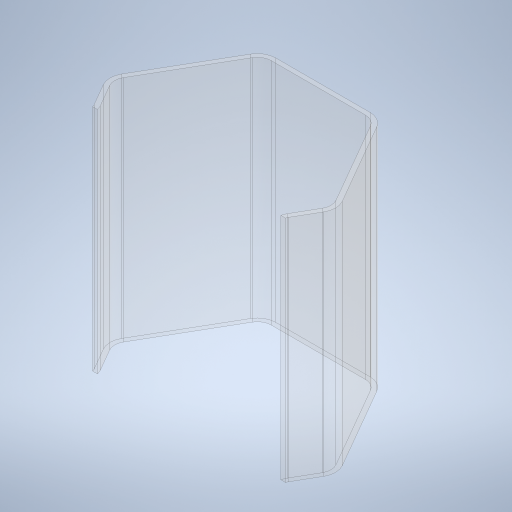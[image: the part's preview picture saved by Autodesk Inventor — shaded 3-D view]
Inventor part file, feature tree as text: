
AUTODESK INVENTOR PART (.ipt)
format: ipt  version: 2024 (Build 280153000, 153)  size: 451,584 bytes
history: native  units: mm
features: extrude x9, sketch x9, projected_geometry x3, fillet x1
ambient origin geometry x8: Origin, YZ Plane, XZ Plane, XY Plane, X Axis, Y Axis, Z Axis, Center Point
bodies: Solid1 (feature_tree)
feature tree (22):
  extrude  "Extrusion1"  Depth=10.0mm
  extrude  "Extrusion2"  Depth=20.0mm TaperAngle=0.0deg
  sketch  "Sketch3"  dims[d8=34.0mm d9=5.0mm d10=0.0mm]
  sketch  "Sketch4"  dims[d12=60.0mm d13=360.0deg d14=22.0mm d15=0.0mm]
  extrude  "Extrusion3"  Depth=5.0mm TaperAngle=0.0deg
  extrude  "Extrusion4"  Depth=22.0mm TaperAngle=0.0deg
  extrude  "Extrusion5"  Depth=20.0mm TaperAngle=0.0deg
  fillet  "Fillet1"  Radius=150.0mm
  extrude  "Extrusion6"  Depth=12.0mm
  extrude  "Extrusion7"  Depth=20.0mm
  extrude  "Extrusion8"  Depth=12.0mm
  extrude  "Extrusion9"  Depth=200.0mm TaperAngle=360.0deg
  sketch  "Sketch1"  dims[d0=250.0mm d1=160.0mm d2=160.0mm d3=10.0mm d4=52.0mm]
  sketch  "Sketch2"  dims[d5=80.0mm d6=20.0mm d7=0.0mm]
  sketch  "Sketch5"  dims[d17=60.0mm d18=360.0deg d19=20.0mm d20=0.0mm d21=150.0mm]
  sketch  "Sketch6"  dims[d22=5.0mm d23=0.0mm d24=12.0mm]
  projected_geometry  "Projected Loop1"
  sketch  "Sketch7"  dims[d25=20.0mm d26=20.0mm]
  sketch  "Sketch8"  dims[d27=12.0mm d28=0.0mm d29=84.286mm]
  projected_geometry  "Projected Loop2"
  sketch  "Sketch9"  dims[d30=10.0mm d31=240.0mm d33=360.0deg d35=39.0mm d36=0.0mm d37=4.0mm d38=200.0mm d39=0.0mm d40=200.0mm d41=0.0mm]
  projected_geometry  "Projected Loop3"
